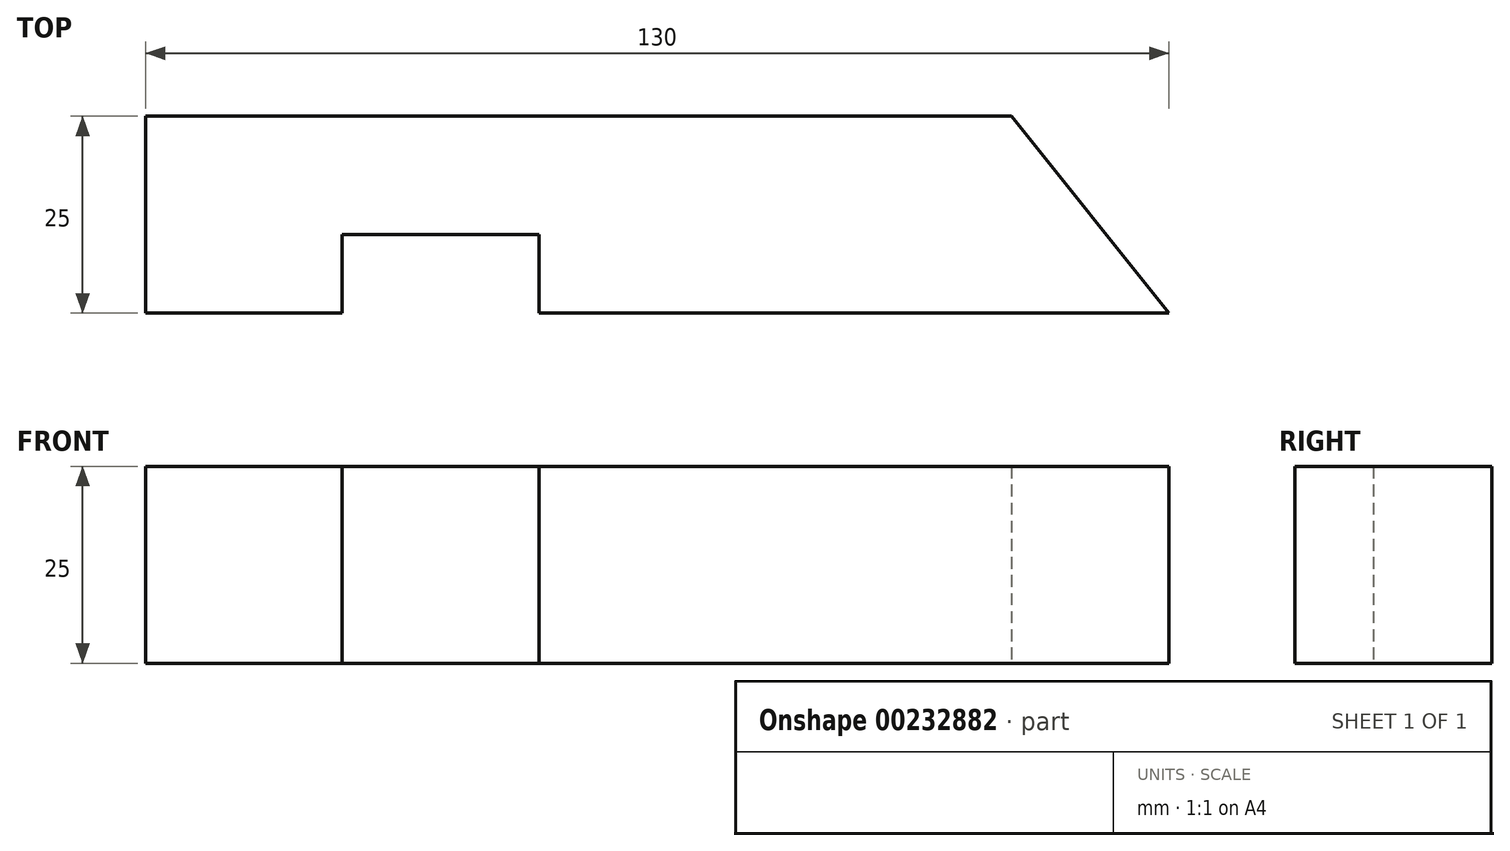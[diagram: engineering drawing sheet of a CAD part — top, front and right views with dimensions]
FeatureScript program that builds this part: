
annotation { "Feature Type Name" : "Feature", "Feature Type Description" : "" }
export const myFeature = defineFeature(function(context is Context, id is Id, definition is map)
    precondition{}
    {
        {
            var Q0;
            Q0=qCreatedBy(makeId("Top.planeOp"),FACE);
            var sketch = newSketch(context, id + "F0", { "sketchPlane" : qUnion([Q0])});
            skLineSegment(sketch, "E0", {"start": v(-61.41, 53.04) * mm, "end": v(48.59, 53.04) * mm});
            skLineSegment(sketch, "E1", {"start": v(-61.41, 53.04) * mm, "end": v(-61.41, 28.04) * mm});
            skLineSegment(sketch, "E2", {"start": v(-61.41, 28.04) * mm, "end": v(-36.41, 28.04) * mm});
            skLineSegment(sketch, "E3", {"start": v(-36.41, 28.04) * mm, "end": v(-36.41, 38.04) * mm});
            skLineSegment(sketch, "E4", {"start": v(-36.41, 38.04) * mm, "end": v(-11.41, 38.04) * mm});
            skLineSegment(sketch, "E5", {"start": v(-11.41, 38.04) * mm, "end": v(-11.41, 28.04) * mm});
            skLineSegment(sketch, "E6", {"start": v(-11.41, 28.04) * mm, "end": v(68.59, 28.04) * mm});
            skLineSegment(sketch, "E7", {"start": v(48.59, 53.04) * mm, "end": v(68.59, 28.04) * mm});
            skSolve(sketch);
        }
        {
            var Q0;
            Q0=makeQuery(id+"F0.imprint","IMPRINT",FACE,{"disambiguationData":[TD([[makeQuery(id+"F0.imprint","IMPRINT",EDGE,{"derivedFrom":sQuery(id+"F0.wireOp",EDGE,"E0")}),-1.0]])]});
            extrude(context, id + "F1", {"entities" : qUnion([Q0]), "depth" : 25 * mm});
        }
    });
